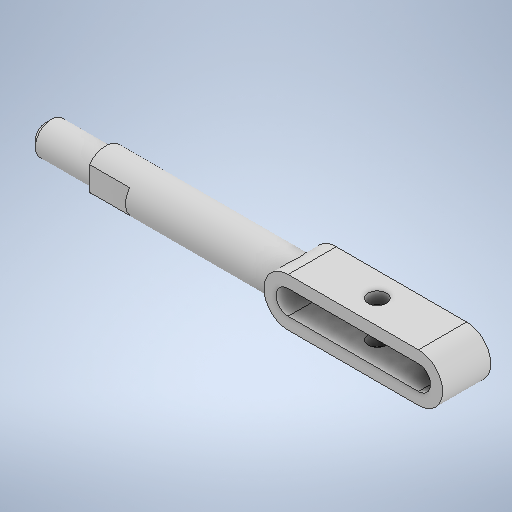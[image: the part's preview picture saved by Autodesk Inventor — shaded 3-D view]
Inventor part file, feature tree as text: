
AUTODESK INVENTOR PART (.ipt)
format: ipt  version: 2025 (Build 290162000, 162)  size: 299,520 bytes
history: native  units: mm
features: sketch x8, extrude x7, plane x3, hole x1, chamfer x1
ambient origin geometry x8: Origin, YZ Plane, XZ Plane, XY Plane, X Axis, Y Axis, Z Axis, Center Point
bodies: Solid1 (feature_tree)
feature tree (20):
  extrude  "Extrusion1"  Depth=24.0mm
  extrude  "Extrusion2"  Depth=12.0mm
  hole  "Hole1"  [1 undecoded]
  plane  "Work Plane1"
  extrude  "Extrusion3"  Depth=20.0mm
  extrude  "Extrusion4"  Depth=16.0mm
  extrude  "Extrusion5"  Depth=3.0mm TaperAngle=45.0deg
  chamfer  "Chamfer1"  Distance=2.0mm
  plane  "Work Plane2"
  extrude  "Extrusion6"  Depth=20.0mm
  plane  "Work Plane3"
  extrude  "Extrusion7"  Depth=20.0mm TaperAngle=0.0deg
  sketch  "Sketch1"  dims[d0=65.0mm d1=24.0mm]
  sketch  "Sketch2"  dims[d2=24.0mm d3=0.0mm d4=12.0mm]
  sketch  "Sketch3"  dims[d5=0.0mm d6=0.0mm]
  sketch  "Sketch4"  dims[d7=9.0mm d8=6.0mm d9=4.0mm d10=2.0mm d11=90.0deg d12=8.0mm d13=20.594885mm d14=20.0mm]
  sketch  "Sketch5"  dims[d15=6.0mm d16=0.0mm d17=20.0mm]
  sketch  "Sketch6"  dims[d18=91.0mm d19=0.0mm d20=16.0mm]
  sketch  "Sketch7"  dims[d21=30.0mm d22=0.0mm d23=3.0mm d24=2.0mm d25=45.0deg]
  sketch  "Sketch8"  dims[d26=20.0mm d27=2.0mm d28=0.0mm d29=20.0mm d30=2.0mm d31=0.0mm]
note: 1 required parameter value undecoded (feature->parameter linkage not recoverable at this tier; creation-order binding heuristic only, values carry confidence <= 0.55)
